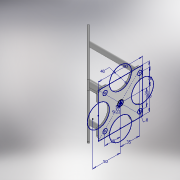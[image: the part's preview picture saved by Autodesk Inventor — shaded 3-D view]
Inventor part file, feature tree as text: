
AUTODESK INVENTOR PART (.ipt)
format: ipt  version: 2017 (Build 210142000, 142)  size: 243,712 bytes
history: native  units: mm
features: extrude x8, sketch x2, chamfer x1, fillet x1
ambient origin geometry x8: Origin, YZ Plane, XZ Plane, XY Plane, X Axis, Y Axis, Z Axis, Center Point
bodies: Solid1 (feature_tree)
feature tree (12):
  extrude  "Extrusion1"  Depth=10.0mm TaperAngle=45.0deg
  chamfer  "Chamfer1"  Distance=4.0mm
  sketch  "Sketch2"  dims[d8=50.0mm d10=4.0mm d11=5.0mm d12=100.0mm d13=0.0mm d14=3.0mm d15=30.0mm d16=30.0mm d17=35.0mm d18=28.0mm d19=8.0mm d20=3.0mm d21=0.0mm d22=5.0mm d23=0.0mm d24=10.0mm d25=3.0mm d26=45.0deg d27=100.0mm d28=80.0mm d29=80.0mm d32=5.0mm d33=0.0mm d34=8.0mm d35=9.22mm d38=40.0mm d39=10.0mm d40=0.0mm d41=8.25mm d42=0.0mm d43=6.22mm d44=0.0mm]
  extrude  "Extrusion2"  Depth=6.22mm
  extrude  "Extrusion3"  Depth=100.0mm TaperAngle=0.0deg
  extrude  "Extrusion4"  Depth=3.0mm
  extrude  "Extrusion5"  Depth=6.22mm
  fillet  "Fillet2"  Radius=30.0mm
  extrude  "Extrusion7"  Depth=35.0mm
  extrude  "Extrusion8"  Depth=6.22mm
  extrude  "Extrusion9"  Depth=8.0mm
  sketch  "Sketch1"  dims[d3=100.0mm d4=0.0mm d5=10.0mm d6=2.0mm d7=45.0deg]
